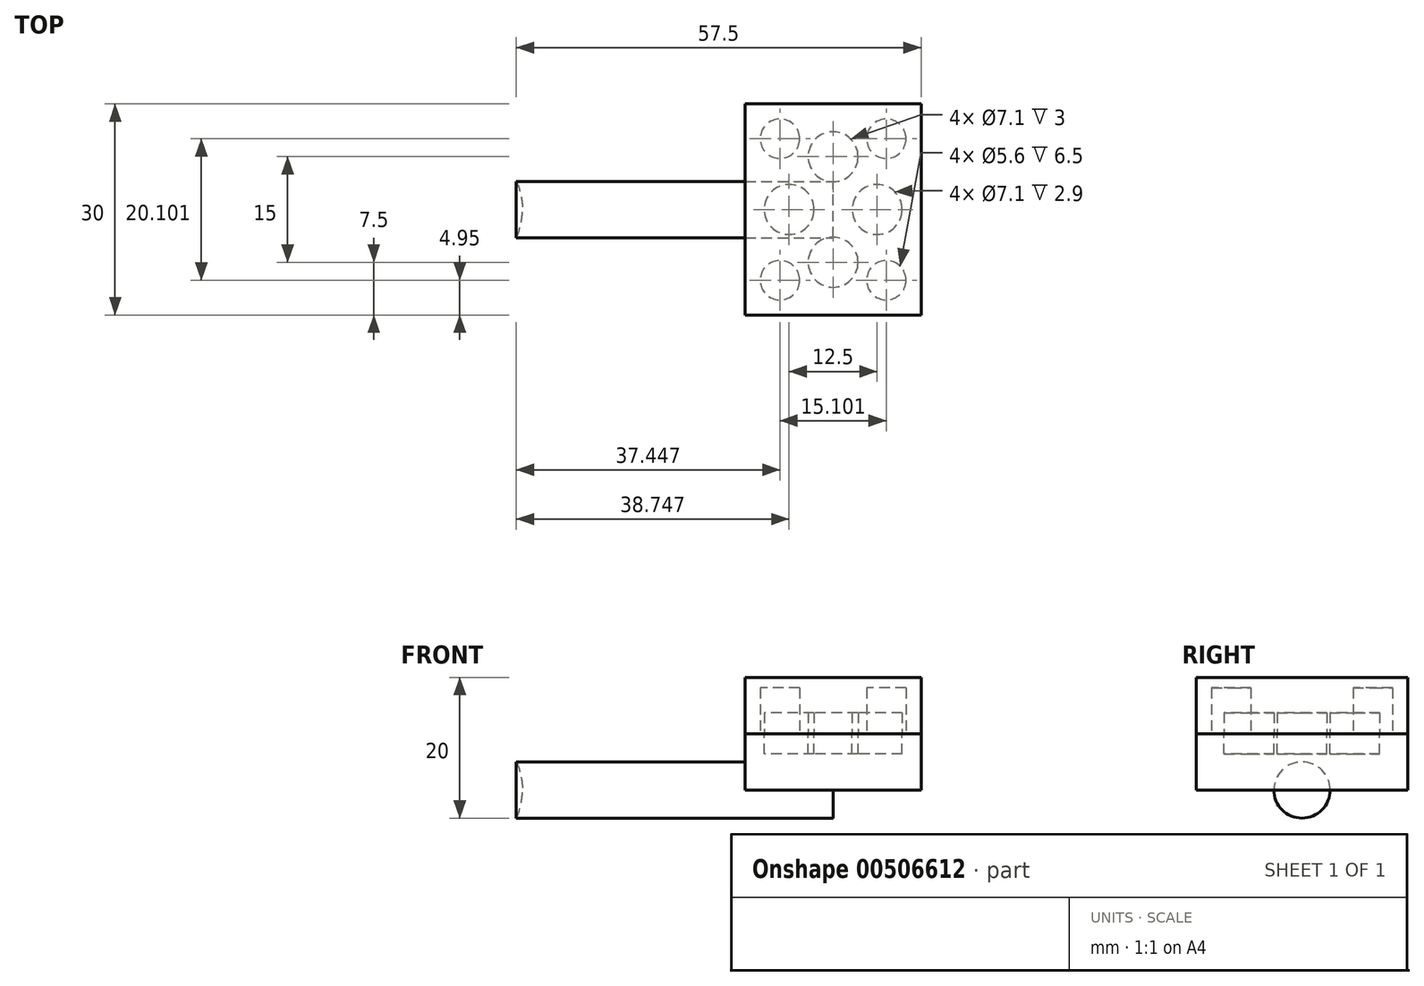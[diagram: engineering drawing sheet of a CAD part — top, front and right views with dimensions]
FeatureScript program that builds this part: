
annotation { "Feature Type Name" : "Feature", "Feature Type Description" : "" }
export const myFeature = defineFeature(function(context is Context, id is Id, definition is map)
    precondition{}
    {
        {
            var Q0;
            Q0=qCreatedBy(makeId("Top.planeOp"),FACE);
            var sketch = newSketch(context, id + "F0", { "sketchPlane" : qUnion([Q0])});
            skArc(sketch, "E0", {"start": v(8.62, 4) * mm, "mid": v(-2.05, 9.28) * mm, "end": v(-9.5, 0) * mm});
            skLineSegment(sketch, "E1.bottom", {"start": v(8.62, 4) * mm, "end": v(53.62, 4) * mm});
            skLineSegment(sketch, "E1.right", {"start": v(53.62, 4) * mm, "end": v(53.62, 0) * mm});
            skLineSegment(sketch, "E2", {"start": v(53.62, -10.05) * mm, "end": v(53.62, -4) * mm, "construction": true});
            skLineSegment(sketch, "E3", {"start": v(53.62, 0) * mm, "end": v(-9.5, 0) * mm});
            skSolve(sketch);
        }
        {
            var Q0;
            Q0=makeQuery(id+"F0.imprint","IMPRINT",FACE,{"disambiguationData":[TD([[makeQuery(id+"F0.imprint","IMPRINT",EDGE,{"derivedFrom":sQuery(id+"F0.wireOp",EDGE,"E0")}),1.0]])]});
            var Q1;
            Q1=sQuery(id+"F0.wireOp",EDGE,"E3");
            revolve(context, id + "F1", {"entities" : qUnion([Q0]), "axis" : qUnion([Q1]), "revolveType" : RevolveType.FULL});
        }
        {
            var Q0;
            Q0=qCreatedBy(makeId("Top.planeOp"),FACE);
            var sketch = newSketch(context, id + "F2", { "sketchPlane" : qUnion([Q0])});
            skLineSegment(sketch, "E4", {"start": v(53.62, -4) * mm, "end": v(8.62, -4) * mm});
            skLineSegment(sketch, "E5", {"start": v(6.12, 4) * mm, "end": v(53.62, 4) * mm});
            skLineSegment(sketch, "E6", {"start": v(53.62, -13.35) * mm, "end": v(53.62, 14.34) * mm, "construction": true});
            skLineSegment(sketch, "E7.bottom", {"start": v(66.12, 15) * mm, "end": v(41.12, 15) * mm});
            skLineSegment(sketch, "E7.top", {"start": v(66.12, -15) * mm, "end": v(41.12, -15) * mm});
            skLineSegment(sketch, "E7.left", {"start": v(66.12, 15) * mm, "end": v(66.12, -15) * mm});
            skLineSegment(sketch, "E7.right", {"start": v(41.12, 15) * mm, "end": v(41.12, -15) * mm});
            skPoint(sketch, "E7.middle", {"position": v(53.62, 0) * mm});
            skSolve(sketch);
        }
        {
            var Q0;
            {var subQ0=sQuery(id+"F2.wireOp",EDGE,"E7.bottom");Q0=makeQuery(id+"F2.imprint","IMPRINT",FACE,{"disambiguationData":[TD([[makeQuery(id+"F2.imprint","IMPRINT",EDGE,{"derivedFrom":subQ0}),1.0]])]});}
            extrude(context, id + "F3", {"entities" : qUnion([Q0]), "operationType" : NewBodyOperationType.ADD, "depth" : 8 * mm});
        }
        {
            var Q0;
            Q0=makeQuery(id+"F3.opExtrude","CAP_FACE",FACE,{"disambiguationData":[OSD([sQuery(id+"F2.wireOp",EDGE,"E7.bottom"),sQuery(id+"F2.wireOp",EDGE,"E7.top"),sQuery(id+"F2.wireOp",EDGE,"E7.left"),sQuery(id+"F2.wireOp",EDGE,"E7.right")])],"isStart":false});
            var sketch = newSketch(context, id + "F4", { "sketchPlane" : qUnion([Q0])});
            skLineSegment(sketch, "E8.0.0", {"start": v(41.12, 15) * mm, "end": v(41.12, -15) * mm});
            skLineSegment(sketch, "E8.0.1", {"start": v(41.12, -15) * mm, "end": v(66.12, -15) * mm});
            skLineSegment(sketch, "E8.0.2", {"start": v(66.12, -15) * mm, "end": v(66.12, 15) * mm});
            skLineSegment(sketch, "E8.0.3", {"start": v(66.12, 15) * mm, "end": v(41.12, 15) * mm});
            skCircle(sketch, "E9", {"center": v(53.62, 7.5) * mm, "radius": 3.55 * mm});
            skLineSegment(sketch, "E10", {"start": v(53.62, 15) * mm, "end": v(53.62, -15) * mm, "construction": true});
            skLineSegment(sketch, "E11", {"start": v(66.12, 0) * mm, "end": v(41.12, 0) * mm, "construction": true});
            skLineSegment(sketch, "E12", {"start": v(41.12, 15) * mm, "end": v(66.12, 0) * mm, "construction": true});
            skLineSegment(sketch, "E13", {"start": v(66.12, 0) * mm, "end": v(41.12, -15) * mm, "construction": true});
            skLineSegment(sketch, "E14", {"start": v(53.62, 15) * mm, "end": v(41.12, -15) * mm, "construction": true});
            skLineSegment(sketch, "E15", {"start": v(53.62, 15) * mm, "end": v(66.12, -15) * mm, "construction": true});
            skCircle(sketch, "E16", {"center": v(47.37, 0) * mm, "radius": 3.55 * mm});
            skCircle(sketch, "E17", {"center": v(59.87, 0) * mm, "radius": 3.55 * mm});
            skCircle(sketch, "E18", {"center": v(53.62, -7.5) * mm, "radius": 3.55 * mm});
            skLineSegment(sketch, "E19", {"start": v(41.12, -15) * mm, "end": v(46.07, -10.05) * mm, "construction": true});
            skCircle(sketch, "E20", {"center": v(46.07, -10.05) * mm, "radius": 2.5 * mm});
            skLineSegment(sketch, "E21", {"start": v(41.12, 15) * mm, "end": v(46.07, 10.05) * mm, "construction": true});
            skLineSegment(sketch, "E22", {"start": v(66.12, 15) * mm, "end": v(61.17, 10.05) * mm, "construction": true});
            skLineSegment(sketch, "E23", {"start": v(66.12, -15) * mm, "end": v(61.17, -10.05) * mm, "construction": true});
            skCircle(sketch, "E24", {"center": v(46.07, 10.05) * mm, "radius": 2.5 * mm});
            skCircle(sketch, "E25", {"center": v(61.17, 10.05) * mm, "radius": 2.5 * mm});
            skCircle(sketch, "E26", {"center": v(61.17, -10.05) * mm, "radius": 2.5 * mm});
            skSolve(sketch);
        }
        {
            var Q0;
            Q0=makeQuery(id+"F4.imprint","IMPRINT",FACE,{"disambiguationData":[TD([[makeQuery(id+"F4.imprint","IMPRINT",EDGE,{"derivedFrom":sQuery(id+"F4.wireOp",EDGE,"E9")}),1.0]])]});
            var Q1;
            Q1=makeQuery(id+"F4.imprint","IMPRINT",FACE,{"disambiguationData":[TD([[makeQuery(id+"F4.imprint","IMPRINT",EDGE,{"derivedFrom":sQuery(id+"F4.wireOp",EDGE,"E16")}),1.0]])]});
            var Q2;
            Q2=makeQuery(id+"F4.imprint","IMPRINT",FACE,{"disambiguationData":[TD([[makeQuery(id+"F4.imprint","IMPRINT",EDGE,{"derivedFrom":sQuery(id+"F4.wireOp",EDGE,"E17")}),1.0]])]});
            var Q3;
            Q3=makeQuery(id+"F4.imprint","IMPRINT",FACE,{"disambiguationData":[TD([[makeQuery(id+"F4.imprint","IMPRINT",EDGE,{"derivedFrom":sQuery(id+"F4.wireOp",EDGE,"E18")}),1.0]])]});
            extrude(context, id + "F5", {"entities" : qUnion([Q0, Q1, Q2, Q3]), "operationType" : NewBodyOperationType.REMOVE, "oppositeDirection" : true, "depth" : 2.9 * mm});
        }
        {
            var Q0;
            Q0=makeQuery(id+"F4.imprint","IMPRINT",FACE,{"disambiguationData":[TD([[makeQuery(id+"F4.imprint","IMPRINT",EDGE,{"derivedFrom":sQuery(id+"F4.wireOp",EDGE,"E24")}),1.0]])]});
            var Q1;
            Q1=makeQuery(id+"F4.imprint","IMPRINT",FACE,{"disambiguationData":[TD([[makeQuery(id+"F4.imprint","IMPRINT",EDGE,{"derivedFrom":sQuery(id+"F4.wireOp",EDGE,"E25")}),1.0]])]});
            var Q2;
            Q2=makeQuery(id+"F4.imprint","IMPRINT",FACE,{"disambiguationData":[TD([[makeQuery(id+"F4.imprint","IMPRINT",EDGE,{"derivedFrom":sQuery(id+"F4.wireOp",EDGE,"E26")}),1.0]])]});
            var Q3;
            Q3=makeQuery(id+"F4.imprint","IMPRINT",FACE,{"disambiguationData":[TD([[makeQuery(id+"F4.imprint","IMPRINT",EDGE,{"derivedFrom":sQuery(id+"F4.wireOp",EDGE,"E20")}),1.0]])]});
            extrude(context, id + "F6", {"entities" : qUnion([Q0, Q1, Q2, Q3]), "operationType" : NewBodyOperationType.ADD, "depth" : 6 * mm});
        }
        {
            var Q0;
            Q0=makeQuery(id+"F6.opExtrude","CAP_EDGE",EDGE,{"disambiguationData":[OSD([sQuery(id+"F4.wireOp",EDGE,"E24")])],"isStart":false});
            var Q1;
            Q1=makeQuery(id+"F6.opExtrude","CAP_EDGE",EDGE,{"disambiguationData":[OSD([sQuery(id+"F4.wireOp",EDGE,"E25")])],"isStart":false});
            var Q2;
            Q2=makeQuery(id+"F6.opExtrude","CAP_EDGE",EDGE,{"disambiguationData":[OSD([sQuery(id+"F4.wireOp",EDGE,"E26")])],"isStart":false});
            var Q3;
            Q3=makeQuery(id+"F6.opExtrude","CAP_EDGE",EDGE,{"disambiguationData":[OSD([sQuery(id+"F4.wireOp",EDGE,"E20")])],"isStart":false});
            chamfer(context, id + "F7", {"entities" : qUnion([Q0, Q1, Q2, Q3]), "width" : 2 * mm, "tangentPropagation" : true});
        }
        {
            var Q0;
            Q0=makeQuery(id+"F4.imprint","IMPRINT",FACE,{"disambiguationData":[TD([[makeQuery(id+"F4.imprint","IMPRINT",EDGE,{"derivedFrom":sQuery(id+"F4.wireOp",EDGE,"E8.0.0")}),1.0]])]});
            var sketch = newSketch(context, id + "F8", { "sketchPlane" : qUnion([Q0])});
            skCircle(sketch, "E27.0", {"center": v(47.37, 0) * mm, "radius": 3.55 * mm});
            skLineSegment(sketch, "E27.1.0", {"start": v(66.12, 15) * mm, "end": v(41.12, 15) * mm});
            skLineSegment(sketch, "E27.1.1", {"start": v(41.12, 15) * mm, "end": v(41.12, -15) * mm});
            skLineSegment(sketch, "E27.1.2", {"start": v(41.12, -15) * mm, "end": v(66.12, -15) * mm});
            skLineSegment(sketch, "E27.1.3", {"start": v(66.12, -15) * mm, "end": v(66.12, 15) * mm});
            skCircle(sketch, "E28.0", {"center": v(53.62, 7.5) * mm, "radius": 3.55 * mm});
            skCircle(sketch, "E28.1", {"center": v(59.87, 0) * mm, "radius": 3.55 * mm});
            skCircle(sketch, "E28.2", {"center": v(53.62, -7.5) * mm, "radius": 3.55 * mm});
            skCircle(sketch, "E29.0", {"center": v(61.17, 10.05) * mm, "radius": 2.5 * mm, "construction": true});
            skCircle(sketch, "E29.1", {"center": v(61.17, -10.05) * mm, "radius": 2.5 * mm, "construction": true});
            skCircle(sketch, "E29.2", {"center": v(46.07, -10.05) * mm, "radius": 2.5 * mm, "construction": true});
            skCircle(sketch, "E30.0", {"center": v(46.07, 10.05) * mm, "radius": 2.5 * mm, "construction": true});
            skCircle(sketch, "E31.0", {"center": v(46.07, 10.05) * mm, "radius": 2.8 * mm});
            skCircle(sketch, "E32.0", {"center": v(61.17, 10.05) * mm, "radius": 2.8 * mm});
            skCircle(sketch, "E33.0", {"center": v(46.07, -10.05) * mm, "radius": 2.8 * mm});
            skCircle(sketch, "E34.0", {"center": v(61.17, -10.05) * mm, "radius": 2.8 * mm});
            skSolve(sketch);
        }
        {
            var Q0;
            Q0=makeQuery(id+"F8.imprint","IMPRINT",FACE,{"disambiguationData":[TD([[makeQuery(id+"F8.imprint","IMPRINT",EDGE,{"derivedFrom":sQuery(id+"F8.wireOp",EDGE,"E27.0")}),-1.0]])]});
            var Q1;
            Q1=makeQuery(id+"F8.imprint","IMPRINT",FACE,{"disambiguationData":[TD([[makeQuery(id+"F8.imprint","IMPRINT",EDGE,{"derivedFrom":makeQuery(id+"F4.imprint","IMPRINT",EDGE,{"derivedFrom":sQuery(id+"F4.wireOp",EDGE,"E24")})}),1.0]])]});
            var Q2;
            Q2=makeQuery(id+"F8.imprint","IMPRINT",FACE,{"disambiguationData":[TD([[makeQuery(id+"F8.imprint","IMPRINT",EDGE,{"derivedFrom":sQuery(id+"F8.wireOp",EDGE,"E31.0")}),1.0]])]});
            var Q3;
            Q3=makeQuery(id+"F8.imprint","IMPRINT",FACE,{"disambiguationData":[TD([[makeQuery(id+"F8.imprint","IMPRINT",EDGE,{"derivedFrom":sQuery(id+"F8.wireOp",EDGE,"E28.0")}),1.0]])]});
            var Q4;
            Q4=makeQuery(id+"F8.imprint","IMPRINT",FACE,{"disambiguationData":[TD([[makeQuery(id+"F8.imprint","IMPRINT",EDGE,{"derivedFrom":sQuery(id+"F8.wireOp",EDGE,"E28.1")}),1.0]])]});
            var Q5;
            Q5=makeQuery(id+"F8.imprint","IMPRINT",FACE,{"disambiguationData":[TD([[makeQuery(id+"F8.imprint","IMPRINT",EDGE,{"derivedFrom":sQuery(id+"F8.wireOp",EDGE,"E28.2")}),1.0]])]});
            var Q6;
            Q6=makeQuery(id+"F8.imprint","IMPRINT",FACE,{"disambiguationData":[TD([[makeQuery(id+"F8.imprint","IMPRINT",EDGE,{"derivedFrom":sQuery(id+"F8.wireOp",EDGE,"E27.0")}),1.0]])]});
            var Q7;
            Q7=makeQuery(id+"F8.imprint","IMPRINT",FACE,{"disambiguationData":[TD([[makeQuery(id+"F8.imprint","IMPRINT",EDGE,{"derivedFrom":sQuery(id+"F8.wireOp",EDGE,"E32.0")}),1.0]])]});
            var Q8;
            Q8=makeQuery(id+"F8.imprint","IMPRINT",FACE,{"disambiguationData":[TD([[makeQuery(id+"F8.imprint","IMPRINT",EDGE,{"derivedFrom":makeQuery(id+"F4.imprint","IMPRINT",EDGE,{"derivedFrom":sQuery(id+"F4.wireOp",EDGE,"E25")})}),1.0]])]});
            var Q9;
            Q9=makeQuery(id+"F8.imprint","IMPRINT",FACE,{"disambiguationData":[TD([[makeQuery(id+"F8.imprint","IMPRINT",EDGE,{"derivedFrom":makeQuery(id+"F4.imprint","IMPRINT",EDGE,{"derivedFrom":sQuery(id+"F4.wireOp",EDGE,"E26")})}),1.0]])]});
            var Q10;
            Q10=makeQuery(id+"F8.imprint","IMPRINT",FACE,{"disambiguationData":[TD([[makeQuery(id+"F8.imprint","IMPRINT",EDGE,{"derivedFrom":sQuery(id+"F8.wireOp",EDGE,"E34.0")}),1.0]])]});
            var Q11;
            Q11=makeQuery(id+"F8.imprint","IMPRINT",FACE,{"disambiguationData":[TD([[makeQuery(id+"F8.imprint","IMPRINT",EDGE,{"derivedFrom":makeQuery(id+"F4.imprint","IMPRINT",EDGE,{"derivedFrom":sQuery(id+"F4.wireOp",EDGE,"E20")})}),1.0]])]});
            var Q12;
            Q12=makeQuery(id+"F8.imprint","IMPRINT",FACE,{"disambiguationData":[TD([[makeQuery(id+"F8.imprint","IMPRINT",EDGE,{"derivedFrom":sQuery(id+"F8.wireOp",EDGE,"E33.0")}),1.0]])]});
            extrude(context, id + "F9", {"entities" : qUnion([Q0, Q1, Q2, Q3, Q4, Q5, Q6, Q7, Q8, Q9, Q10, Q11, Q12]), "depth" : 8 * mm});
        }
        {
            var Q0;
            Q0=makeQuery(id+"F8.imprint","IMPRINT",FACE,{"disambiguationData":[TD([[makeQuery(id+"F8.imprint","IMPRINT",EDGE,{"derivedFrom":sQuery(id+"F8.wireOp",EDGE,"E28.0")}),1.0]])]});
            var Q1;
            Q1=makeQuery(id+"F8.imprint","IMPRINT",FACE,{"disambiguationData":[TD([[makeQuery(id+"F8.imprint","IMPRINT",EDGE,{"derivedFrom":sQuery(id+"F8.wireOp",EDGE,"E28.1")}),1.0]])]});
            var Q2;
            Q2=makeQuery(id+"F8.imprint","IMPRINT",FACE,{"disambiguationData":[TD([[makeQuery(id+"F8.imprint","IMPRINT",EDGE,{"derivedFrom":sQuery(id+"F8.wireOp",EDGE,"E27.0")}),1.0]])]});
            var Q3;
            Q3=makeQuery(id+"F8.imprint","IMPRINT",FACE,{"disambiguationData":[TD([[makeQuery(id+"F8.imprint","IMPRINT",EDGE,{"derivedFrom":sQuery(id+"F8.wireOp",EDGE,"E28.2")}),1.0]])]});
            extrude(context, id + "F10", {"entities" : qUnion([Q0, Q1, Q2, Q3]), "operationType" : NewBodyOperationType.REMOVE, "depth" : 3 * mm});
        }
        {
            var Q0;
            Q0=makeQuery(id+"F8.imprint","IMPRINT",FACE,{"disambiguationData":[TD([[makeQuery(id+"F8.imprint","IMPRINT",EDGE,{"derivedFrom":makeQuery(id+"F4.imprint","IMPRINT",EDGE,{"derivedFrom":sQuery(id+"F4.wireOp",EDGE,"E20")})}),1.0]])]});
            var Q1;
            Q1=makeQuery(id+"F8.imprint","IMPRINT",FACE,{"disambiguationData":[TD([[makeQuery(id+"F8.imprint","IMPRINT",EDGE,{"derivedFrom":makeQuery(id+"F4.imprint","IMPRINT",EDGE,{"derivedFrom":sQuery(id+"F4.wireOp",EDGE,"E24")})}),1.0]])]});
            var Q2;
            Q2=makeQuery(id+"F8.imprint","IMPRINT",FACE,{"disambiguationData":[TD([[makeQuery(id+"F8.imprint","IMPRINT",EDGE,{"derivedFrom":makeQuery(id+"F4.imprint","IMPRINT",EDGE,{"derivedFrom":sQuery(id+"F4.wireOp",EDGE,"E25")})}),1.0]])]});
            var Q3;
            Q3=makeQuery(id+"F8.imprint","IMPRINT",FACE,{"disambiguationData":[TD([[makeQuery(id+"F8.imprint","IMPRINT",EDGE,{"derivedFrom":makeQuery(id+"F4.imprint","IMPRINT",EDGE,{"derivedFrom":sQuery(id+"F4.wireOp",EDGE,"E26")})}),1.0]])]});
            var Q4;
            Q4=makeQuery(id+"F8.imprint","IMPRINT",FACE,{"disambiguationData":[TD([[makeQuery(id+"F8.imprint","IMPRINT",EDGE,{"derivedFrom":sQuery(id+"F8.wireOp",EDGE,"E31.0")}),1.0]])]});
            var Q5;
            Q5=makeQuery(id+"F8.imprint","IMPRINT",FACE,{"disambiguationData":[TD([[makeQuery(id+"F8.imprint","IMPRINT",EDGE,{"derivedFrom":sQuery(id+"F8.wireOp",EDGE,"E32.0")}),1.0]])]});
            var Q6;
            Q6=makeQuery(id+"F8.imprint","IMPRINT",FACE,{"disambiguationData":[TD([[makeQuery(id+"F8.imprint","IMPRINT",EDGE,{"derivedFrom":sQuery(id+"F8.wireOp",EDGE,"E33.0")}),1.0]])]});
            var Q7;
            Q7=makeQuery(id+"F8.imprint","IMPRINT",FACE,{"disambiguationData":[TD([[makeQuery(id+"F8.imprint","IMPRINT",EDGE,{"derivedFrom":sQuery(id+"F8.wireOp",EDGE,"E34.0")}),1.0]])]});
            extrude(context, id + "F11", {"entities" : qUnion([Q0, Q1, Q2, Q3, Q4, Q5, Q6, Q7]), "operationType" : NewBodyOperationType.REMOVE, "depth" : 6.5 * mm});
        }
    });
